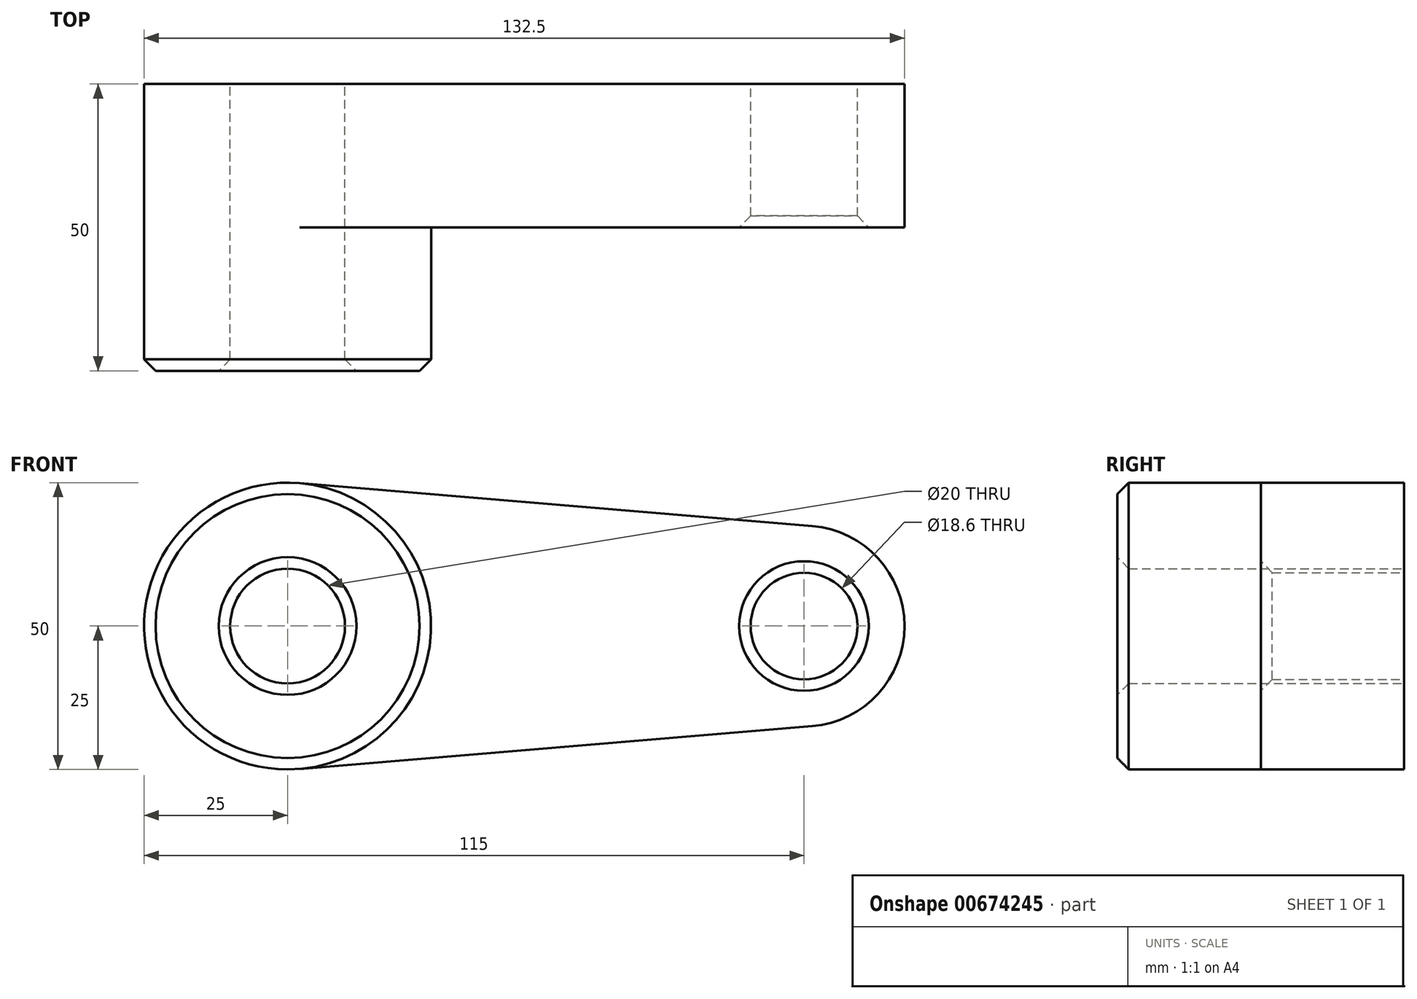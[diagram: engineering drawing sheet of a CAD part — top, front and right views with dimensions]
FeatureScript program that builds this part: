
annotation { "Feature Type Name" : "Feature", "Feature Type Description" : "" }
export const myFeature = defineFeature(function(context is Context, id is Id, definition is map)
    precondition{}
    {
        {
            var Q0;
            Q0=qCreatedBy(makeId("Front.planeOp"),FACE);
            var sketch = newSketch(context, id + "F0", { "sketchPlane" : qUnion([Q0])});
            skCircle(sketch, "E0", {"center": v(0, 0) * mm, "radius": 25 * mm});
            skCircle(sketch, "E1", {"center": v(90, 0) * mm, "radius": 17.5 * mm});
            skLineSegment(sketch, "E2", {"start": v(2.08, 24.91) * mm, "end": v(91.46, 17.44) * mm});
            skLineSegment(sketch, "E3", {"start": v(2.08, -24.91) * mm, "end": v(91.46, -17.44) * mm});
            skCircle(sketch, "E4", {"center": v(0, 0) * mm, "radius": 10 * mm});
            skCircle(sketch, "E5", {"center": v(90, 0) * mm, "radius": 9.3 * mm});
            skSolve(sketch);
        }
        {
            var Q0;
            Q0 = qSketchRegion(id + "F0", true);
            extrude(context, id + "F1", {"entities" : qUnion([Q0]), "depth" : 25 * mm, "offsetDistance" : 25 * mm});
        }
        {
            var Q0;
            Q0=makeQuery(id+"F0.imprint","IMPRINT",FACE,{"disambiguationData":[TD([[makeQuery(id+"F0.imprint","IMPRINT",EDGE,{"derivedFrom":sQuery(id+"F0.wireOp",EDGE,"E4")}),-1.0]])]});
            var Q1;
            Q1=sQuery(id+"F0.wireOp",EDGE,"E0");
            extrude(context, id + "F2", {"entities" : qUnion([Q0]), "operationType" : NewBodyOperationType.ADD, "surfaceEntities" : qUnion([Q1]), "depth" : 50 * mm, "offsetDistance" : 25 * mm});
        }
        {
            var Q0;
            Q0=makeQuery(id+"F1.opExtrude","CAP_EDGE",EDGE,{"disambiguationData":[OSD([sQuery(id+"F0.wireOp",EDGE,"E5")])],"isStart":false});
            var Q1;
            Q1=makeQuery(id+"F2.opExtrude","CAP_EDGE",EDGE,{"disambiguationData":[OSD([sQuery(id+"F0.wireOp",EDGE,"E4")])],"isStart":false});
            var Q2;
            Q2=makeQuery(id+"F2.opExtrude","CAP_EDGE",EDGE,{"disambiguationData":[OSD([sQuery(id+"F0.wireOp",EDGE,"E0")])],"isStart":false});
            chamfer(context, id + "F3", {"entities" : qUnion([Q0, Q1, Q2]), "width" : 2 * mm, "tangentPropagation" : true});
        }
    });
